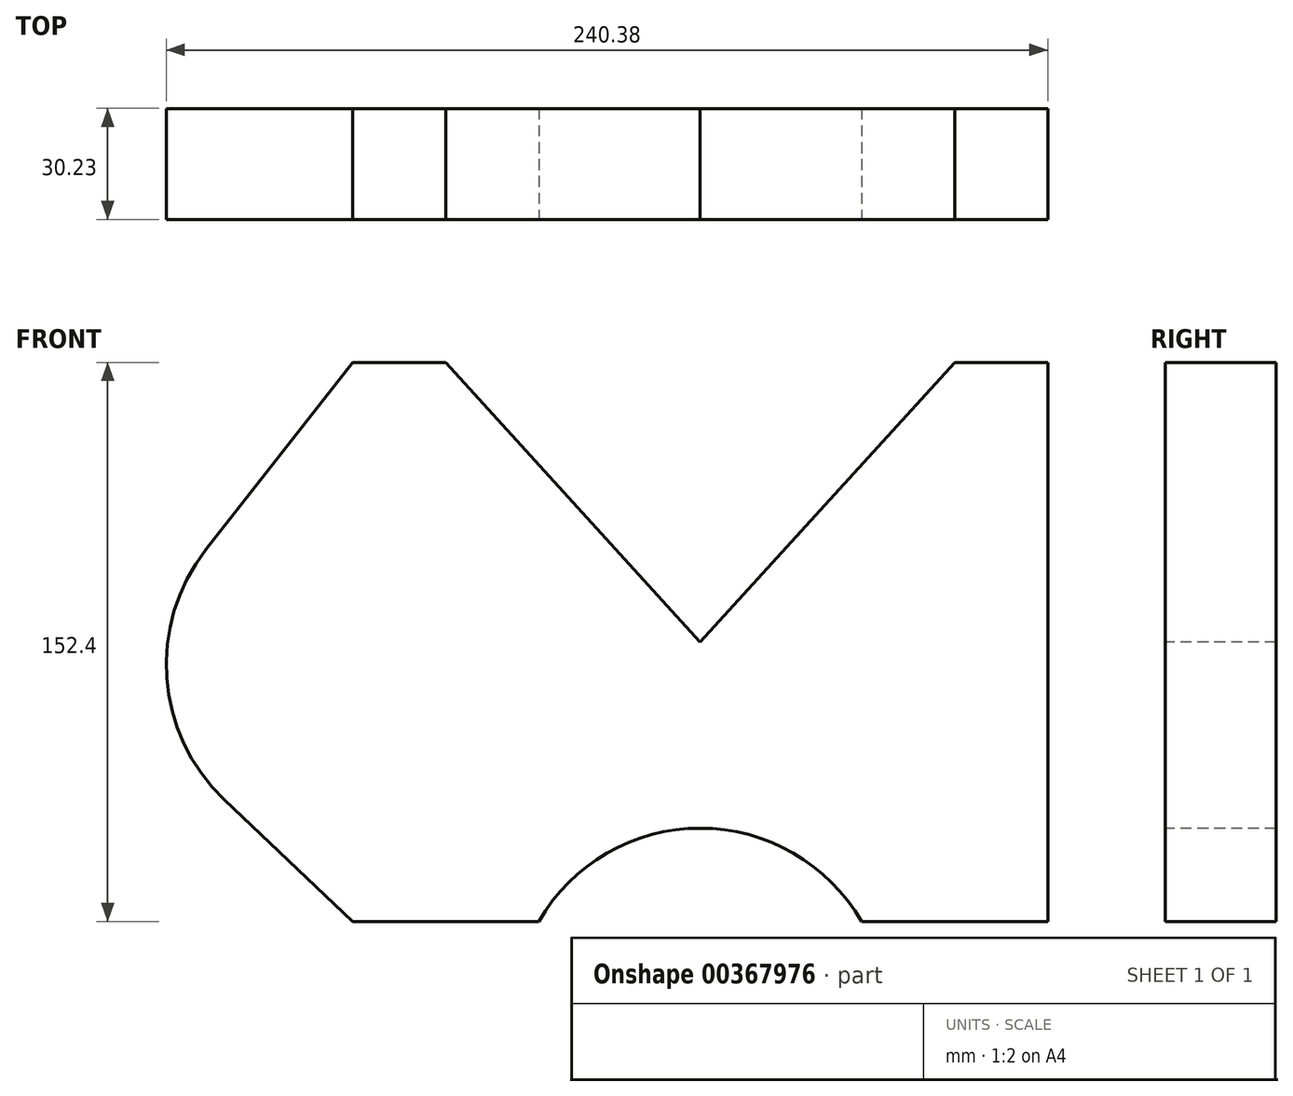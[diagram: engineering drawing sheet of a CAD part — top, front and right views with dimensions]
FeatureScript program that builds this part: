
annotation { "Feature Type Name" : "Feature", "Feature Type Description" : "" }
export const myFeature = defineFeature(function(context is Context, id is Id, definition is map)
    precondition{}
    {
        {
            var Q0;
            Q0=qCreatedBy(makeId("Front.planeOp"),FACE);
            var sketch = newSketch(context, id + "F0", { "sketchPlane" : qUnion([Q0])});
            skLineSegment(sketch, "E0", {"start": v(0, 0) * mm, "end": v(69.4, 76.2) * mm});
            skLineSegment(sketch, "E1", {"start": v(69.4, 76.2) * mm, "end": v(94.8, 76.2) * mm});
            skLineSegment(sketch, "E2", {"start": v(94.8, 76.2) * mm, "end": v(94.8, -76.2) * mm});
            skLineSegment(sketch, "E3", {"start": v(94.8, -76.2) * mm, "end": v(44, -76.2) * mm});
            skArc(sketch, "E4", {"start": v(44, -76.2) * mm, "mid": v(0, -50.8) * mm, "end": v(-44, -76.2) * mm});
            skLineSegment(sketch, "E5", {"start": v(-44, -76.2) * mm, "end": v(-94.8, -76.2) * mm});
            skLineSegment(sketch, "E6", {"start": v(-94.8, -76.2) * mm, "end": v(-129.77, -43) * mm});
            skLineSegment(sketch, "E7", {"start": v(0, 0) * mm, "end": v(-69.4, 76.2) * mm});
            skLineSegment(sketch, "E8", {"start": v(-69.4, 76.2) * mm, "end": v(-94.8, 76.2) * mm});
            skLineSegment(sketch, "E9", {"start": v(-94.8, 76.2) * mm, "end": v(-134.78, 25.18) * mm});
            skArc(sketch, "E10", {"start": v(-134.78, 25.18) * mm, "mid": v(-145.46, -9.88) * mm, "end": v(-129.77, -43) * mm});
            skSolve(sketch);
        }
        {
            var Q0;
            Q0=makeQuery(id+"F0.imprint","IMPRINT",FACE,{"disambiguationData":[TD([[makeQuery(id+"F0.imprint","IMPRINT",EDGE,{"derivedFrom":sQuery(id+"F0.wireOp",EDGE,"E0")}),-1.0]])]});
            extrude(context, id + "F1", {"entities" : qUnion([Q0]), "oppositeDirection" : true, "depth" : 30.23 * mm});
        }
    });
